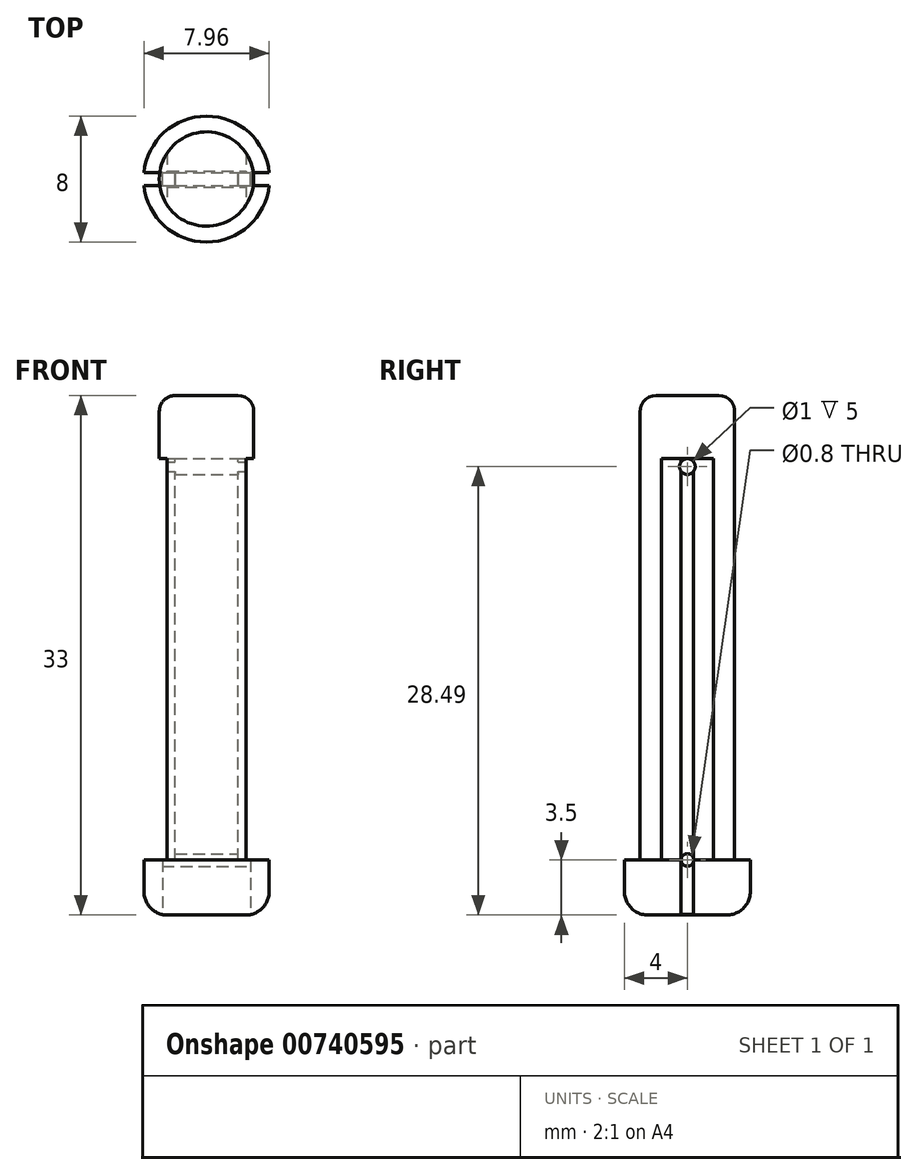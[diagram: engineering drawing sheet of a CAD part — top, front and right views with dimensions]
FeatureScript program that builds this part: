
annotation { "Feature Type Name" : "Feature", "Feature Type Description" : "" }
export const myFeature = defineFeature(function(context is Context, id is Id, definition is map)
    precondition{}
    {
        {
            var Q0;
            Q0=qCreatedBy(makeId("Front.planeOp"),FACE);
            var sketch = newSketch(context, id + "F0", { "sketchPlane" : qUnion([Q0])});
            skLineSegment(sketch, "E0", {"start": v(0, -18) * mm, "end": v(4, -18) * mm});
            skLineSegment(sketch, "E1", {"start": v(4, -18) * mm, "end": v(4, -14.5) * mm});
            skLineSegment(sketch, "E2", {"start": v(4, -14.5) * mm, "end": v(3, -14.5) * mm});
            skLineSegment(sketch, "E3", {"start": v(3, -14.5) * mm, "end": v(3, 15) * mm});
            skLineSegment(sketch, "E4", {"start": v(3, 15) * mm, "end": v(0, 15) * mm});
            skLineSegment(sketch, "E5", {"start": v(0, 15) * mm, "end": v(0, -18) * mm});
            skSolve(sketch);
        }
        {
            var Q0;
            Q0=makeQuery(id+"F0.imprint","IMPRINT",FACE,{"disambiguationData":[TD([[makeQuery(id+"F0.imprint","IMPRINT",EDGE,{"derivedFrom":sQuery(id+"F0.wireOp",EDGE,"E0")}),1.0]])]});
            var Q1;
            Q1=sQuery(id+"F0.wireOp",EDGE,"E5");
            revolve(context, id + "F1", {"surfaceOperationType" : NewSurfaceOperationType.NEW, "entities" : qUnion([Q0]), "axis" : qUnion([Q1]), "revolveType" : RevolveType.FULL});
        }
        {
            var Q0;
            Q0=makeQuery(id+"F1.opRevolve","SWEPT_EDGE",EDGE,{"disambiguationData":[OSD([sQuery(id+"F0.wireOp",EDGE,"E3"),sQuery(id+"F0.wireOp",EDGE,"E4")])]});
            fillet(context, id + "F2", {"entities" : qUnion([Q0]), "radius" : 1 * mm, "tangentPropagation" : true, "allowEdgeOverflow" : false});
        }
        {
            var Q0;
            Q0=makeQuery(id+"F1.opRevolve","SWEPT_EDGE",EDGE,{"disambiguationData":[OSD([sQuery(id+"F0.wireOp",EDGE,"E0"),sQuery(id+"F0.wireOp",EDGE,"E1")])]});
            fillet(context, id + "F3", {"entities" : qUnion([Q0]), "radius" : 1.5 * mm, "tangentPropagation" : true, "allowEdgeOverflow" : false});
        }
        {
            var Q0;
            Q0=qCreatedBy(makeId("Front.planeOp"),FACE);
            var sketch = newSketch(context, id + "F4", { "sketchPlane" : qUnion([Q0])});
            skLineSegment(sketch, "E6.0", {"start": v(-4, -14.5) * mm, "end": v(4, -14.5) * mm});
            skLineSegment(sketch, "E7", {"start": v(-2.5, -14.5) * mm, "end": v(-2.5, 11) * mm});
            skLineSegment(sketch, "E8", {"start": v(-2.5, 11) * mm, "end": v(-4, 11) * mm});
            skLineSegment(sketch, "E9", {"start": v(-4, 11) * mm, "end": v(-4, -14.5) * mm});
            skLineSegment(sketch, "E10", {"start": v(2.5, -14.5) * mm, "end": v(2.5, 11) * mm});
            skLineSegment(sketch, "E11", {"start": v(2.5, 11) * mm, "end": v(4, 11) * mm});
            skLineSegment(sketch, "E12", {"start": v(4, 11) * mm, "end": v(4, -14.5) * mm});
            skSolve(sketch);
        }
        {
            var Q0;
            {var subQ2=sQuery(id+"F4.wireOp",EDGE,"E7");Q0=makeQuery(id+"F4.imprint","IMPRINT",FACE,{"disambiguationData":[TD([[makeQuery(id+"F4.imprint","IMPRINT",EDGE,{"derivedFrom":subQ2}),1.0]])]});}
            var Q1;
            {var subQ2=sQuery(id+"F4.wireOp",EDGE,"E10");Q1=makeQuery(id+"F4.imprint","IMPRINT",FACE,{"disambiguationData":[TD([[makeQuery(id+"F4.imprint","IMPRINT",EDGE,{"derivedFrom":subQ2}),-1.0]])]});}
            extrude(context, id + "F5", {"entities" : qUnion([Q0, Q1]), "operationType" : NewBodyOperationType.REMOVE, "oppositeDirection" : true, "depth" : 25 * mm, "offsetDistance" : 25 * mm, "hasSecondDirection" : true, "secondDirectionOppositeDirection" : false, "secondDirectionDepth" : 25 * mm});
        }
        {
            var Q0;
            Q0=makeQuery(id+"F1.opRevolve","SWEPT_FACE",FACE,{"disambiguationData":[OSD([sQuery(id+"F0.wireOp",EDGE,"E0")])]});
            var sketch = newSketch(context, id + "F6", { "sketchPlane" : qUnion([Q0])});
            skLineSegment(sketch, "E13.bottom", {"start": v(-5.08, 0.4) * mm, "end": v(-2.8, 0.4) * mm});
            skLineSegment(sketch, "E13.top", {"start": v(-5.08, -0.4) * mm, "end": v(-2.8, -0.4) * mm});
            skLineSegment(sketch, "E13.left", {"start": v(-5.08, 0.4) * mm, "end": v(-5.08, -0.4) * mm});
            skLineSegment(sketch, "E13.right", {"start": v(-2.8, 0.4) * mm, "end": v(-2.8, -0.4) * mm});
            skPoint(sketch, "E13.middle", {"position": v(-3.94, 0) * mm});
            skLineSegment(sketch, "E14.bottom", {"start": v(4.8, 0.4) * mm, "end": v(2.8, 0.4) * mm});
            skLineSegment(sketch, "E14.top", {"start": v(4.8, -0.4) * mm, "end": v(2.8, -0.4) * mm});
            skLineSegment(sketch, "E14.left", {"start": v(4.8, 0.4) * mm, "end": v(4.8, -0.4) * mm});
            skLineSegment(sketch, "E14.right", {"start": v(2.8, 0.4) * mm, "end": v(2.8, -0.4) * mm});
            skPoint(sketch, "E14.middle", {"position": v(3.8, 0) * mm});
            skSolve(sketch);
        }
        {
            var Q0;
            {var subQ0=sQuery(id+"F6.wireOp",EDGE,"E13.left");Q0=makeQuery(id+"F6.imprint","IMPRINT",FACE,{"disambiguationData":[TD([[makeQuery(id+"F6.imprint","IMPRINT",EDGE,{"derivedFrom":subQ0}),1.0]])]});}
            var Q1;
            {var subQ0=sQuery(id+"F6.wireOp",EDGE,"E13.right");Q1=makeQuery(id+"F6.imprint","IMPRINT",FACE,{"disambiguationData":[TD([[makeQuery(id+"F6.imprint","IMPRINT",EDGE,{"derivedFrom":subQ0}),-1.0]])]});}
            var Q2;
            Q2=makeQuery(id+"F6.imprint","IMPRINT",FACE,{"disambiguationData":[TD([[makeQuery(id+"F6.imprint","IMPRINT",EDGE,{"derivedFrom":sQuery(id+"F6.wireOp",EDGE,"E14.bottom")}),1.0]])]});
            var Q3;
            {var subQ0=sQuery(id+"F4.wireOp",EDGE,"E6.0");Q3=makeQuery(id+"F5.boolean.opBoolean","MERGE",FACE,{"derivedFrom":[makeQuery(id+"F1.opRevolve","SWEPT_FACE",FACE,{"disambiguationData":[OSD([sQuery(id+"F0.wireOp",EDGE,"E2")])]}),makeQuery(id+"F5.opExtrude","SWEPT_FACE",FACE,{"disambiguationData":[OSD([subQ0]),TDD([makeQuery(id+"F4.imprint","IMPRINT",EDGE,{"disambiguationData":[TD([[makeQuery(id+"F4.imprint","INTERSECT",VERTEX,{"derivedFrom":[subQ0,sQuery(id+"F4.wireOp",EDGE,"E9")]}),-1.0]])],"derivedFrom":subQ0})])]}),makeQuery(id+"F5.opExtrude","SWEPT_FACE",FACE,{"disambiguationData":[OSD([subQ0]),TDD([makeQuery(id+"F4.imprint","IMPRINT",EDGE,{"disambiguationData":[TD([[makeQuery(id+"F4.imprint","INTERSECT",VERTEX,{"derivedFrom":[subQ0,sQuery(id+"F4.wireOp",EDGE,"E12")]}),1.0]])],"derivedFrom":subQ0})])]})]});}
            var Q4;
            Q4=makeQuery(id+"F5.boolean.opBoolean","COPY",FACE,{"derivedFrom":makeQuery(id+"F5.opExtrude","SWEPT_FACE",FACE,{"disambiguationData":[OSD([sQuery(id+"F4.wireOp",EDGE,"E8")])]})});
            extrude(context, id + "F7", {"entities" : qUnion([Q0, Q1, Q2, Q3]), "operationType" : NewBodyOperationType.REMOVE, "endBound" : BoundingType.UP_TO_SURFACE, "oppositeDirection" : true, "depth" : 25 * mm, "endBoundEntityFace" : qUnion([Q4]), "offsetDistance" : 25 * mm});
        }
        {
            var Q0;
            Q0=makeQuery(id+"F5.boolean.opBoolean","COPY",FACE,{"derivedFrom":makeQuery(id+"F5.opExtrude","SWEPT_FACE",FACE,{"disambiguationData":[OSD([sQuery(id+"F4.wireOp",EDGE,"E8")])]})});
            var sketch = newSketch(context, id + "F8", { "sketchPlane" : qUnion([Q0])});
            skLineSegment(sketch, "E15.bottom", {"start": v(-3.53, 0.4) * mm, "end": v(-2, 0.4) * mm});
            skLineSegment(sketch, "E15.top", {"start": v(-3.53, -0.4) * mm, "end": v(-2, -0.4) * mm});
            skLineSegment(sketch, "E15.left", {"start": v(-3.53, 0.4) * mm, "end": v(-3.53, -0.4) * mm});
            skLineSegment(sketch, "E15.right", {"start": v(-2, 0.4) * mm, "end": v(-2, -0.4) * mm});
            skPoint(sketch, "E15.middle", {"position": v(-2.76, 0) * mm});
            skPoint(sketch, "E15.middle.positionSnap0", {"position": v(-2.5, 0) * mm});
            skPoint(sketch, "E15.centerSnap0", {"position": v(-2.5, 0) * mm});
            skLineSegment(sketch, "E16.bottom", {"start": v(2, 0.4) * mm, "end": v(4.03, 0.4) * mm});
            skLineSegment(sketch, "E16.top", {"start": v(2, -0.4) * mm, "end": v(4.03, -0.4) * mm});
            skLineSegment(sketch, "E16.left", {"start": v(2, 0.4) * mm, "end": v(2, -0.4) * mm});
            skLineSegment(sketch, "E16.right", {"start": v(4.03, 0.4) * mm, "end": v(4.03, -0.4) * mm});
            skPoint(sketch, "E16.middle", {"position": v(3.02, 0) * mm});
            skSolve(sketch);
        }
        {
            var Q0;
            Q0 = qSketchRegion(id + "F8", true);
            var Q1;
            {var subQ0=sQuery(id+"F4.wireOp",EDGE,"E6.0");Q1=makeQuery(id+"F5.boolean.opBoolean","MERGE",FACE,{"derivedFrom":[makeQuery(id+"F1.opRevolve","SWEPT_FACE",FACE,{"disambiguationData":[OSD([sQuery(id+"F0.wireOp",EDGE,"E2")])]}),makeQuery(id+"F5.opExtrude","SWEPT_FACE",FACE,{"disambiguationData":[OSD([subQ0]),TDD([makeQuery(id+"F4.imprint","IMPRINT",EDGE,{"disambiguationData":[TD([[makeQuery(id+"F4.imprint","INTERSECT",VERTEX,{"derivedFrom":[subQ0,sQuery(id+"F4.wireOp",EDGE,"E9")]}),-1.0]])],"derivedFrom":subQ0})])]}),makeQuery(id+"F5.opExtrude","SWEPT_FACE",FACE,{"disambiguationData":[OSD([subQ0]),TDD([makeQuery(id+"F4.imprint","IMPRINT",EDGE,{"disambiguationData":[TD([[makeQuery(id+"F4.imprint","INTERSECT",VERTEX,{"derivedFrom":[subQ0,sQuery(id+"F4.wireOp",EDGE,"E12")]}),1.0]])],"derivedFrom":subQ0})])]})]});}
            extrude(context, id + "F9", {"entities" : qUnion([Q0]), "operationType" : NewBodyOperationType.REMOVE, "endBound" : BoundingType.UP_TO_SURFACE, "depth" : 25 * mm, "endBoundEntityFace" : qUnion([Q1]), "offsetDistance" : 25 * mm});
        }
        {
            var Q0;
            Q0=qCreatedBy(makeId("Right.planeOp"),FACE);
            var sketch = newSketch(context, id + "F10", { "sketchPlane" : qUnion([Q0])});
            skLineSegment(sketch, "E17.0", {"start": v(0.4, -14.5) * mm, "end": v(4, -14.5) * mm, "construction": true});
            skCircle(sketch, "E18", {"center": v(0, -14.5) * mm, "radius": 0.4 * mm});
            skCircle(sketch, "E19", {"center": v(0, 10.5) * mm, "radius": 0.5 * mm});
            skSolve(sketch);
        }
        {
            var Q0;
            Q0 = qSketchRegion(id + "F10", true);
            extrude(context, id + "F11", {"entities" : qUnion([Q0]), "operationType" : NewBodyOperationType.REMOVE, "endBound" : BoundingType.THROUGH_ALL, "oppositeDirection" : true, "depth" : 25 * mm, "offsetDistance" : 25 * mm, "hasSecondDirection" : true, "secondDirectionOppositeDirection" : false, "secondDirectionDepth" : 25 * mm});
        }
    });
